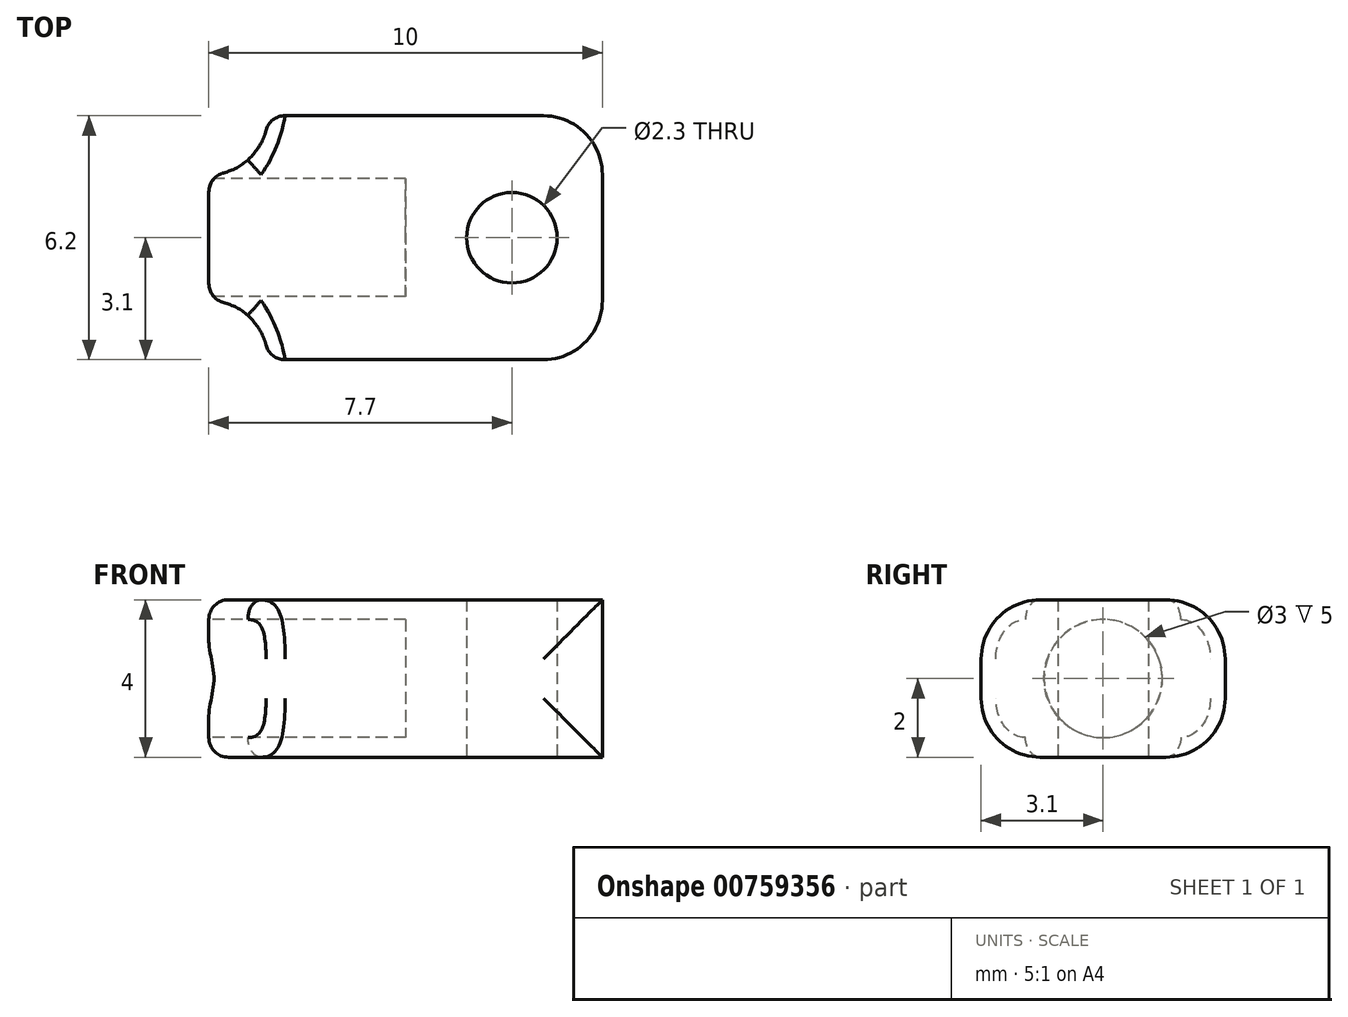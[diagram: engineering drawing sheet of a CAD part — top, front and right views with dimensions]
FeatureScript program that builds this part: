
annotation { "Feature Type Name" : "Feature", "Feature Type Description" : "" }
export const myFeature = defineFeature(function(context is Context, id is Id, definition is map)
    precondition{}
    {
        {
            var Q0;
            Q0=qCreatedBy(makeId("Top.planeOp"),FACE);
            var sketch = newSketch(context, id + "F0", { "sketchPlane" : qUnion([Q0])});
            skLineSegment(sketch, "E0.bottom", {"start": v(-3.5, 3.1) * mm, "end": v(5, 3.1) * mm});
            skLineSegment(sketch, "E0.top", {"start": v(-3.5, -3.1) * mm, "end": v(5, -3.1) * mm});
            skLineSegment(sketch, "E0.left", {"start": v(-5, 1.6) * mm, "end": v(-5, -1.6) * mm});
            skLineSegment(sketch, "E0.right", {"start": v(5, 3.1) * mm, "end": v(5, -3.1) * mm});
            skPoint(sketch, "E0.middle", {"position": v(0, 0) * mm});
            skArc(sketch, "E1", {"start": v(-5, 1.6) * mm, "mid": v(-3.94, 2.04) * mm, "end": v(-3.5, 3.1) * mm});
            skArc(sketch, "E2.MirrorCS", {"start": v(-5, -1.6) * mm, "mid": v(-3.94, -2.04) * mm, "end": v(-3.5, -3.1) * mm});
            skCircle(sketch, "E3", {"center": v(2.7, 0) * mm, "radius": 1.15 * mm});
            skSolve(sketch);
        }
        {
            var Q0;
            Q0 = qSketchRegion(id + "F0", true);
            extrude(context, id + "F1", {"entities" : qUnion([Q0]), "depth" : 4 * mm, "offsetDistance" : 25 * mm});
        }
        {
            var Q0;
            Q0=makeQuery(id+"F1.opExtrude","SWEPT_FACE",FACE,{"disambiguationData":[OSD([sQuery(id+"F0.wireOp",EDGE,"E0.left")])]});
            var sketch = newSketch(context, id + "F2", { "sketchPlane" : qUnion([Q0])});
            skCircle(sketch, "E4", {"center": v(0, 2) * mm, "radius": 1.5 * mm});
            skPoint(sketch, "E4.centerSnap0", {"position": v(-1.6, 2) * mm});
            skSolve(sketch);
        }
        {
            var Q0;
            Q0 = qSketchRegion(id + "F2", true);
            extrude(context, id + "F3", {"entities" : qUnion([Q0]), "operationType" : NewBodyOperationType.REMOVE, "oppositeDirection" : true, "depth" : 5 * mm, "offsetDistance" : 25 * mm});
        }
        {
            var Q0;
            Q0=makeQuery(id+"F1.opExtrude","CAP_EDGE",EDGE,{"disambiguationData":[OSD([sQuery(id+"F0.wireOp",EDGE,"E0.top")])],"isStart":false});
            var Q1;
            Q1=makeQuery(id+"F1.opExtrude","CAP_EDGE",EDGE,{"disambiguationData":[OSD([sQuery(id+"F0.wireOp",EDGE,"E0.top")])],"isStart":true});
            var Q2;
            Q2=makeQuery(id+"F1.opExtrude","SWEPT_EDGE",EDGE,{"disambiguationData":[OSD([sQuery(id+"F0.wireOp",EDGE,"E0.top"),sQuery(id+"F0.wireOp",EDGE,"E0.right")])]});
            var Q3;
            Q3=makeQuery(id+"F1.opExtrude","SWEPT_EDGE",EDGE,{"disambiguationData":[OSD([sQuery(id+"F0.wireOp",EDGE,"E0.bottom"),sQuery(id+"F0.wireOp",EDGE,"E0.right")])]});
            var Q4;
            Q4=makeQuery(id+"F1.opExtrude","CAP_EDGE",EDGE,{"disambiguationData":[OSD([sQuery(id+"F0.wireOp",EDGE,"E0.bottom")])],"isStart":false});
            var Q5;
            Q5=makeQuery(id+"F1.opExtrude","CAP_EDGE",EDGE,{"disambiguationData":[OSD([sQuery(id+"F0.wireOp",EDGE,"E0.bottom")])],"isStart":true});
            fillet(context, id + "F4", {"entities" : qUnion([Q0, Q1, Q2, Q3, Q4, Q5]), "radius" : 1.5 * mm, "tangentPropagation" : true, "allowEdgeOverflow" : false});
        }
        {
            var Q0;
            Q0=makeQuery(id+"F1.opExtrude","CAP_EDGE",EDGE,{"disambiguationData":[OSD([sQuery(id+"F0.wireOp",EDGE,"E0.left")])],"isStart":true});
            var Q1;
            {var subQ0=sQuery(id+"F0.wireOp",EDGE,"E0.bottom");Q1=makeQuery(id+"F4.opFillet","BLEND_EDGE",EDGE,{"blendedFrom":[makeQuery(id+"F1.opExtrude","CAP_EDGE",EDGE,{"disambiguationData":[OSD([subQ0])],"isStart":false}),makeQuery(id+"F1.opExtrude","CAP_FACE",FACE,{"disambiguationData":[OSD([subQ0,sQuery(id+"F0.wireOp",EDGE,"E0.top"),sQuery(id+"F0.wireOp",EDGE,"E0.left"),sQuery(id+"F0.wireOp",EDGE,"E0.right"),sQuery(id+"F0.wireOp",EDGE,"E1"),sQuery(id+"F0.wireOp",EDGE,"E2.MirrorCS"),sQuery(id+"F0.wireOp",EDGE,"E3")])],"isStart":false})],"blendedInto":[makeQuery(id+"F1.opExtrude","CAP_FACE",FACE,{"disambiguationData":[OSD([subQ0,sQuery(id+"F0.wireOp",EDGE,"E0.top"),sQuery(id+"F0.wireOp",EDGE,"E0.left"),sQuery(id+"F0.wireOp",EDGE,"E0.right"),sQuery(id+"F0.wireOp",EDGE,"E1"),sQuery(id+"F0.wireOp",EDGE,"E2.MirrorCS"),sQuery(id+"F0.wireOp",EDGE,"E3")])],"isStart":false})]});}
            var Q2;
            Q2=makeQuery(id+"F4.opFillet","BLEND_EDGE",EDGE,{"blendedFrom":[makeQuery(id+"F1.opExtrude","CAP_EDGE",EDGE,{"disambiguationData":[OSD([sQuery(id+"F0.wireOp",EDGE,"E0.top")])],"isStart":false}),makeQuery(id+"F1.opExtrude","SWEPT_FACE",FACE,{"disambiguationData":[OSD([sQuery(id+"F0.wireOp",EDGE,"E2.MirrorCS")])]})],"blendedInto":[makeQuery(id+"F1.opExtrude","SWEPT_FACE",FACE,{"disambiguationData":[OSD([sQuery(id+"F0.wireOp",EDGE,"E2.MirrorCS")])]})]});
            var Q3;
            Q3=makeQuery(id+"F4.opFillet","BLEND_EDGE",EDGE,{"blendedFrom":[makeQuery(id+"F1.opExtrude","CAP_EDGE",EDGE,{"disambiguationData":[OSD([sQuery(id+"F0.wireOp",EDGE,"E0.bottom")])],"isStart":false}),makeQuery(id+"F1.opExtrude","SWEPT_FACE",FACE,{"disambiguationData":[OSD([sQuery(id+"F0.wireOp",EDGE,"E1")])]})],"blendedInto":[makeQuery(id+"F1.opExtrude","SWEPT_FACE",FACE,{"disambiguationData":[OSD([sQuery(id+"F0.wireOp",EDGE,"E1")])]})]});
            fillet(context, id + "F5", {"entities" : qUnion([Q0, Q1, Q2, Q3]), "radius" : .5 * mm, "tangentPropagation" : true, "allowEdgeOverflow" : false});
        }
        {
            var Q0;
            Q0=makeQuery(id+"F1.opExtrude","CAP_EDGE",EDGE,{"disambiguationData":[OSD([sQuery(id+"F0.wireOp",EDGE,"E0.left")])],"isStart":false});
            fillet(context, id + "F6", {"entities" : qUnion([Q0]), "radius" : .5 * mm, "tangentPropagation" : true, "allowEdgeOverflow" : false});
        }
    });
